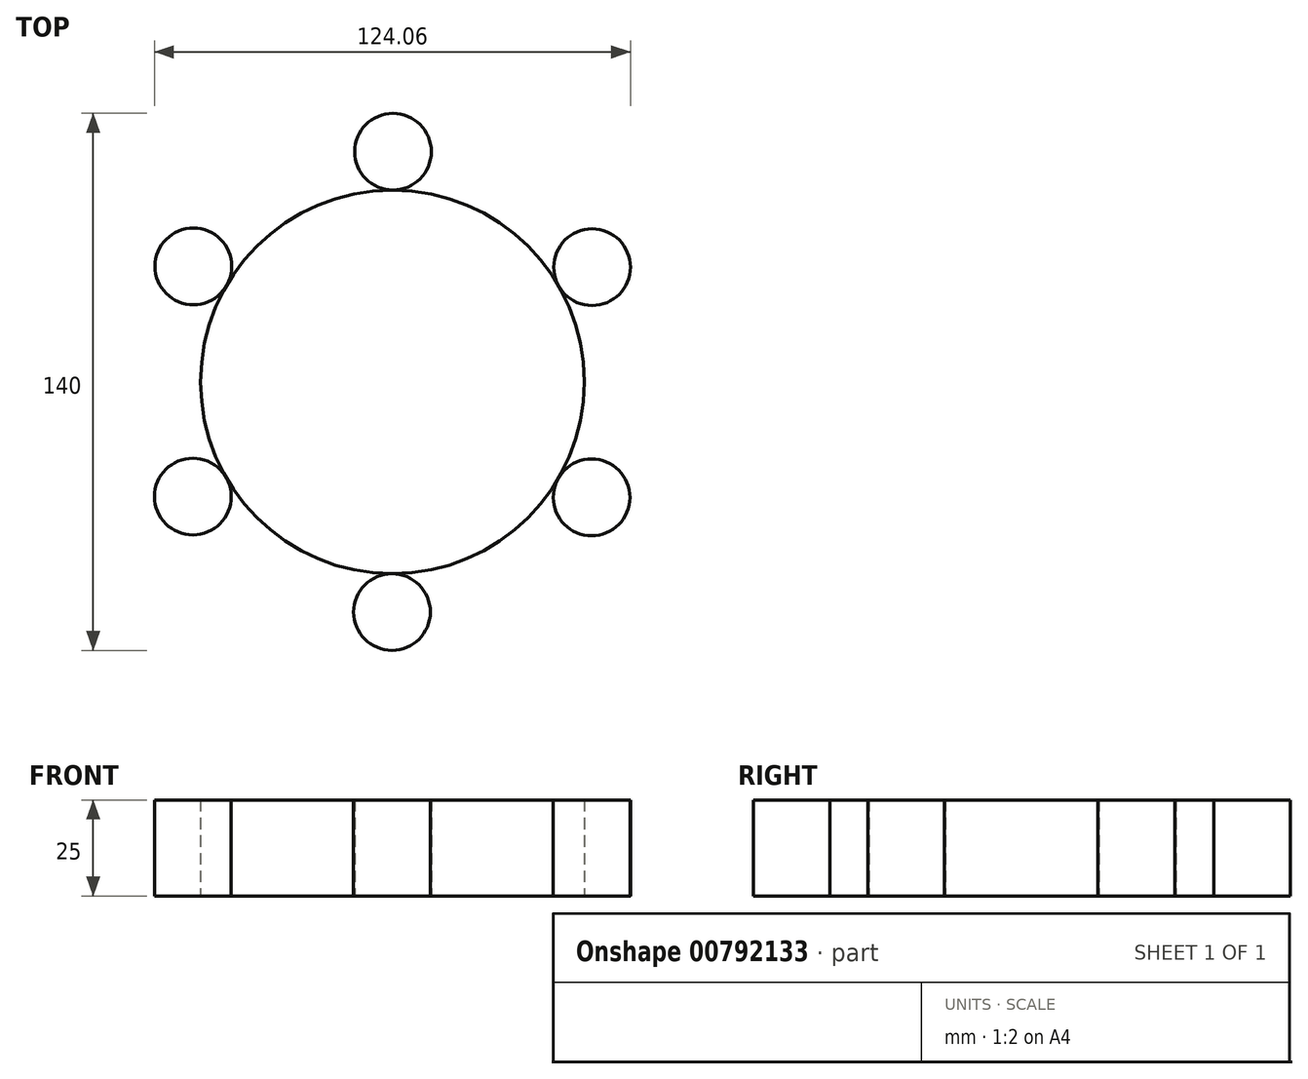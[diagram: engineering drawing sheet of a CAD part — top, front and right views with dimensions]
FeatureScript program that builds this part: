
annotation { "Feature Type Name" : "Feature", "Feature Type Description" : "" }
export const myFeature = defineFeature(function(context is Context, id is Id, definition is map)
    precondition{}
    {
        {
            var Q0;
            Q0=qCreatedBy(makeId("Top.planeOp"),FACE);
            var sketch = newSketch(context, id + "F0", { "sketchPlane" : qUnion([Q0])});
            skCircle(sketch, "E0", {"center": v(-0.13, 5.47) * mm, "radius": 50 * mm});
            skCircle(sketch, "E1", {"center": v(0, 65.47) * mm, "radius": 10 * mm});
            skPoint(sketch, "E2.center", {"position": v(0, 0) * mm});
            skSolve(sketch);
        }
        {
            var Q0;
            {var subQ0=sQuery(id+"F0.wireOp",EDGE,"E0");Q0=makeQuery(id+"F0.imprint","IMPRINT",FACE,{"disambiguationData":[TD([[makeQuery(id+"F0.imprint","IMPRINT",EDGE,{"disambiguationData":[TD([[makeQuery(id+"F0.imprint","INTERSECT",VERTEX,{"derivedFrom":[subQ0,sQuery(id+"F0.wireOp",EDGE,"E1")]}),-1.0]])],"derivedFrom":subQ0}),1.0]])]});}
            extrude(context, id + "F1", {"entities" : qUnion([Q0]), "depth" : 25 * mm, "offsetDistance" : 25 * mm});
        }
        {
            var Q0;
            {var subQ0=sQuery(id+"F0.wireOp",EDGE,"E1");Q0=makeQuery(id+"F0.imprint","IMPRINT",FACE,{"disambiguationData":[TD([[makeQuery(id+"F0.imprint","IMPRINT",EDGE,{"disambiguationData":[TD([[makeQuery(id+"F0.imprint","INTERSECT",VERTEX,{"derivedFrom":[sQuery(id+"F0.wireOp",EDGE,"E0"),subQ0]}),-1.0]])],"derivedFrom":subQ0}),1.0]])]});}
            extrude(context, id + "F2", {"entities" : qUnion([Q0]), "operationType" : NewBodyOperationType.ADD, "depth" : 25 * mm, "offsetDistance" : 25 * mm});
        }
        {
            var Q0;
            Q0=makeQuery(id+"F2.opExtrude","SWEPT_BODY",BODY,{"disambiguationData":[OSD([sQuery(id+"F0.wireOp",EDGE,"E1")])]});
            var Q1;
            Q1=makeQuery(id+"F1.opExtrude","CAP_EDGE",EDGE,{"disambiguationData":[OSD([sQuery(id+"F0.wireOp",EDGE,"E0")])],"isStart":false});
            circularPattern(context, id + "F3", {"entities" : qUnion([Q0]), "axis" : qUnion([Q1]), "angle" : 360 * degree, "instanceCount" : 6, "equalSpace" : true});
        }
    });
